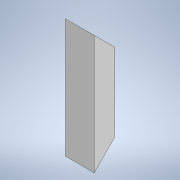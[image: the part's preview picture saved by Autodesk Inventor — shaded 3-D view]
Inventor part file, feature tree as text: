
AUTODESK INVENTOR PART (.ipt)
format: ipt  version: 2020 (Build 240168000, 168)  size: 105,472 bytes
history: native  units: mm
features: extrude x2, sketch x2
ambient origin geometry x8: Origin, YZ Plane, XZ Plane, XY Plane, X Axis, Y Axis, Z Axis, Center Point
bodies: Solid1 (feature_tree)
feature tree (4):
  extrude  "Extrusion1"  Depth=8.485mm
  extrude  "Extrusion4"  TaperAngle=45.0deg  [1 undecoded]
  sketch  "Sketch1"  dims[d0=12.0mm d1=8.485mm]
  sketch  "Sketch5"  dims[d2=50.0mm d3=0.0mm d11=45.0deg d12=12.0mm d13=0.0mm d15=45.0deg]
note: 1 required parameter value undecoded (feature->parameter linkage not recoverable at this tier; creation-order binding heuristic only, values carry confidence <= 0.55)
